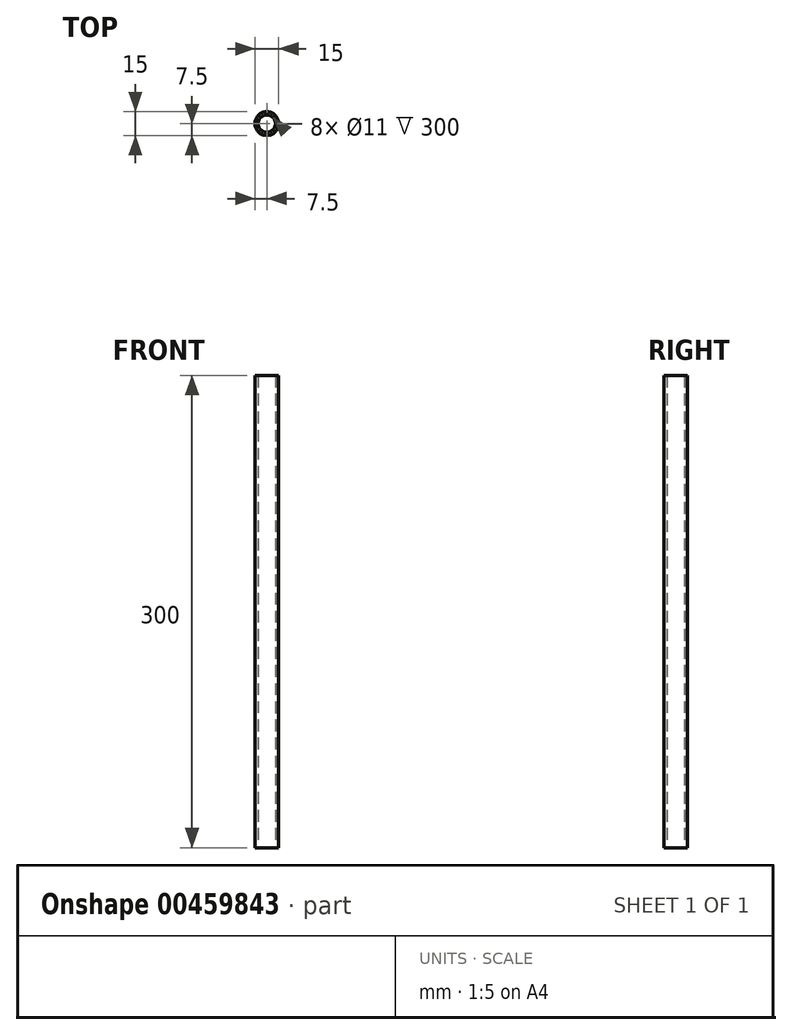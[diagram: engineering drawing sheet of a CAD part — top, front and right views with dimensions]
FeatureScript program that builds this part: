
annotation { "Feature Type Name" : "Feature", "Feature Type Description" : "" }
export const myFeature = defineFeature(function(context is Context, id is Id, definition is map)
    precondition{}
    {
        {
            var Q0;
            Q0=qCreatedBy(makeId("Top.planeOp"),FACE);
            var sketch = newSketch(context, id + "F0", { "sketchPlane" : qUnion([Q0])});
            skCircle(sketch, "E0", {"center": v(0, 0) * mm, "radius": 5.5 * mm});
            skCircle(sketch, "E1", {"center": v(0, 0) * mm, "radius": 7.5 * mm});
            skSolve(sketch);
        }
        {
            var Q0;
            Q0=qSketchRegion(id+"F0",true);
            extrude(context, id + "F1", {"entities" : qUnion([Q0]), "depth" : 300 * mm, "offsetDistance" : 25 * mm});
        }
    });
